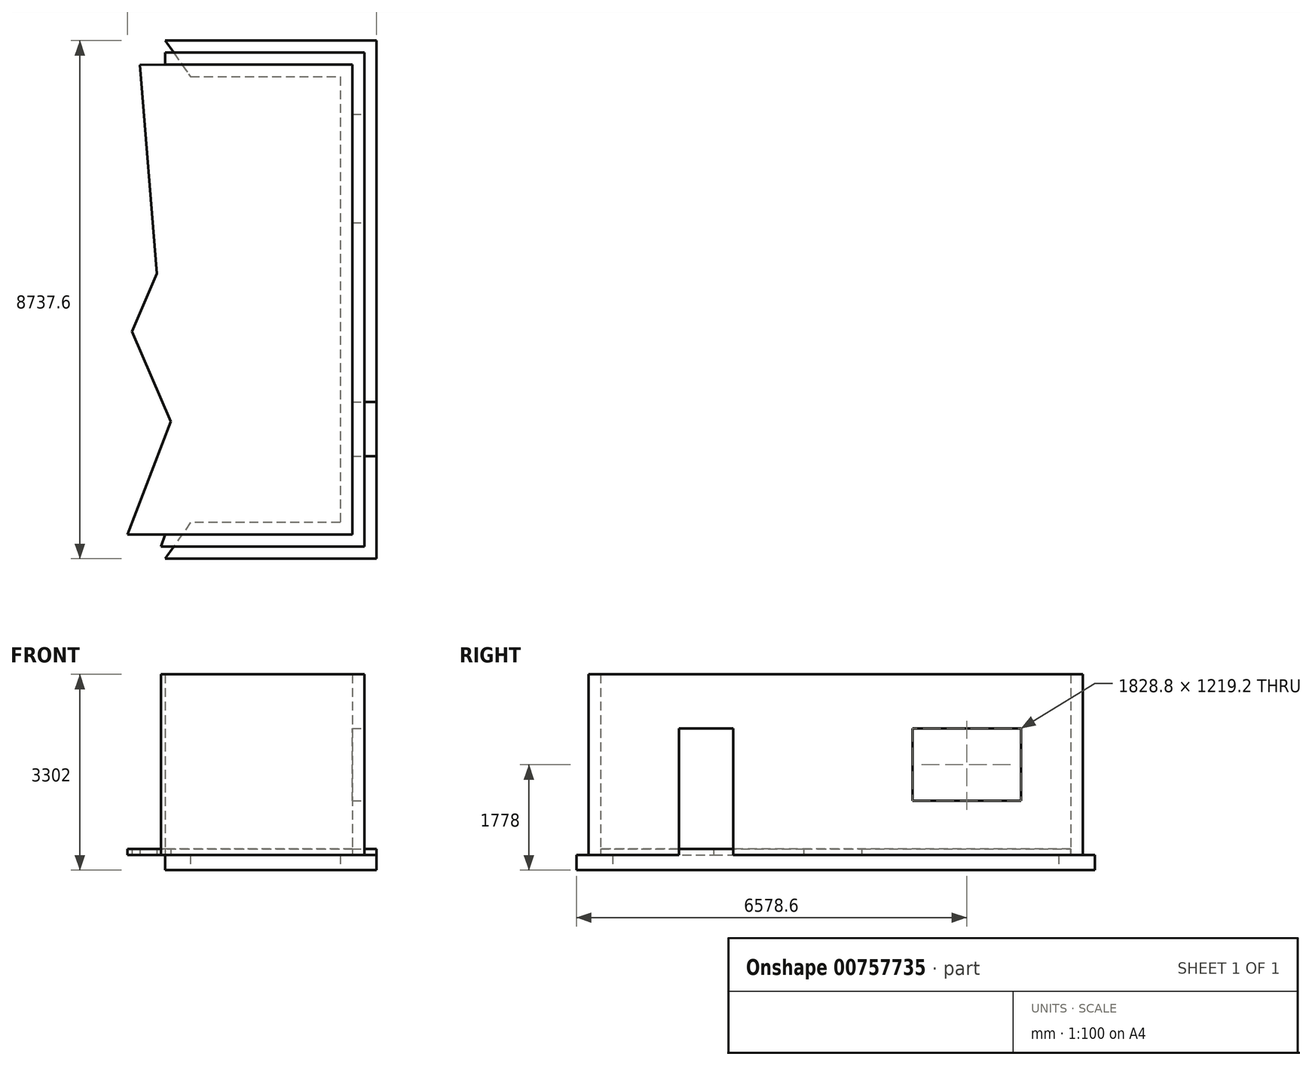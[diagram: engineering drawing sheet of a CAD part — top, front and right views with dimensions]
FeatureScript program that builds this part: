
annotation { "Feature Type Name" : "Feature", "Feature Type Description" : "" }
export const myFeature = defineFeature(function(context is Context, id is Id, definition is map)
    precondition{}
    {
        {
            var Q0;
            Q0=qCreatedBy(makeId("Top.planeOp"),FACE);
            var sketch = newSketch(context, id + "F0", { "sketchPlane" : qUnion([Q0])});
            skLineSegment(sketch, "E0", {"start": v(0, 0) * mm, "end": v(0, 8737.6) * mm});
            skLineSegment(sketch, "E1", {"start": v(0, 8737.6) * mm, "end": v(-3558.04, 8737.6) * mm});
            skLineSegment(sketch, "E2", {"start": v(-3558.04, 8737.6) * mm, "end": v(-3134.22, 8128) * mm});
            skLineSegment(sketch, "E3", {"start": v(-3134.22, 8128) * mm, "end": v(-609.6, 8128) * mm});
            skLineSegment(sketch, "E4", {"start": v(-609.6, 8128) * mm, "end": v(-609.6, 609.6) * mm});
            skLineSegment(sketch, "E5", {"start": v(-609.6, 609.6) * mm, "end": v(-3134.22, 609.6) * mm});
            skLineSegment(sketch, "E6", {"start": v(-3134.22, 609.6) * mm, "end": v(-3558.04, 0) * mm});
            skLineSegment(sketch, "E7", {"start": v(-3558.04, 0) * mm, "end": v(0, 0) * mm});
            skSolve(sketch);
        }
        {
            var Q0;
            Q0 = qSketchRegion(id + "F0", true);
            extrude(context, id + "F1", {"entities" : qUnion([Q0]), "depth" : 254 * mm, "offsetDistance" : 25.4 * mm});
        }
        {
            var Q0;
            Q0=makeQuery(id+"F1.opExtrude","CAP_FACE",FACE,{"disambiguationData":[OSD([sQuery(id+"F0.wireOp",EDGE,"E0"),sQuery(id+"F0.wireOp",EDGE,"E1"),sQuery(id+"F0.wireOp",EDGE,"E2"),sQuery(id+"F0.wireOp",EDGE,"E3"),sQuery(id+"F0.wireOp",EDGE,"E4"),sQuery(id+"F0.wireOp",EDGE,"E5"),sQuery(id+"F0.wireOp",EDGE,"E6"),sQuery(id+"F0.wireOp",EDGE,"E7")])],"isStart":false});
            var sketch = newSketch(context, id + "F2", { "sketchPlane" : qUnion([Q0])});
            skLineSegment(sketch, "E8", {"start": v(-3631.45, 203.2) * mm, "end": v(-203.2, 203.2) * mm});
            skLineSegment(sketch, "E9", {"start": v(-203.2, 203.2) * mm, "end": v(-203.2, 8534.4) * mm});
            skLineSegment(sketch, "E10", {"start": v(-203.2, 8534.4) * mm, "end": v(-3558.04, 8534.4) * mm});
            skLineSegment(sketch, "E11", {"start": v(-3558.04, 8534.4) * mm, "end": v(-3558.04, 8331.2) * mm});
            skLineSegment(sketch, "E12", {"start": v(-3558.04, 8331.2) * mm, "end": v(-406.4, 8331.2) * mm});
            skLineSegment(sketch, "E13", {"start": v(-406.4, 8331.2) * mm, "end": v(-406.4, 406.4) * mm});
            skLineSegment(sketch, "E14", {"start": v(-406.4, 406.4) * mm, "end": v(-3558.04, 406.4) * mm});
            skLineSegment(sketch, "E15", {"start": v(-3558.04, 406.4) * mm, "end": v(-3631.45, 203.2) * mm});
            skSolve(sketch);
        }
        {
            var Q0;
            Q0 = qSketchRegion(id + "F2", true);
            extrude(context, id + "F3", {"entities" : qUnion([Q0]), "operationType" : NewBodyOperationType.ADD, "depth" : 3048 * mm, "offsetDistance" : 25.4 * mm});
        }
        {
            var Q0;
            Q0=makeQuery(id+"F3.opExtrude","SWEPT_FACE",FACE,{"disambiguationData":[OSD([sQuery(id+"F2.wireOp",EDGE,"E9")])]});
            var sketch = newSketch(context, id + "F4", { "sketchPlane" : qUnion([Q0])});
            skLineSegment(sketch, "E16", {"start": v(1727.2, 254) * mm, "end": v(1727.2, 2387.6) * mm});
            skLineSegment(sketch, "E17", {"start": v(1727.2, 2387.6) * mm, "end": v(2641.6, 2387.6) * mm});
            skLineSegment(sketch, "E18", {"start": v(2641.6, 2387.6) * mm, "end": v(2641.6, 254) * mm});
            skLineSegment(sketch, "E19", {"start": v(2641.6, 254) * mm, "end": v(1727.2, 254) * mm});
            skLineSegment(sketch, "E20", {"start": v(5664.2, 2387.6) * mm, "end": v(5664.2, 1168.4) * mm});
            skLineSegment(sketch, "E21", {"start": v(5664.2, 1168.4) * mm, "end": v(7493, 1168.4) * mm});
            skLineSegment(sketch, "E22", {"start": v(7493, 1168.4) * mm, "end": v(7493, 2387.6) * mm});
            skLineSegment(sketch, "E23", {"start": v(7493, 2387.6) * mm, "end": v(5664.2, 2387.6) * mm});
            skSolve(sketch);
        }
        {
            var Q0;
            Q0 = qSketchRegion(id + "F4", true);
            extrude(context, id + "F5", {"entities" : qUnion([Q0]), "operationType" : NewBodyOperationType.REMOVE, "oppositeDirection" : true, "depth" : 203.2 * mm, "offsetDistance" : 25.4 * mm});
        }
        {
            var Q0;
            {var subQ0=sQuery(id+"F0.wireOp",EDGE,"E5");var subQ2=sQuery(id+"F0.wireOp",EDGE,"E4");var subQ3=sQuery(id+"F0.wireOp",EDGE,"E3");var subQ4=sQuery(id+"F0.wireOp",EDGE,"E2");var subQ6=sQuery(id+"F0.wireOp",EDGE,"E6");var subQ14=sQuery(id+"F0.wireOp",EDGE,"E7");var subQ15=sQuery(id+"F0.wireOp",EDGE,"E1");var subQ16=sQuery(id+"F0.wireOp",EDGE,"E0");var subQ17=makeQuery(id+"F1.opExtrude","CAP_FACE",FACE,{"disambiguationData":[OSD([subQ16,subQ15,subQ4,subQ3,subQ2,subQ0,subQ6,subQ14])],"isStart":false});Q0=makeQuery(id+"F5.boolean.opBoolean","MERGE",FACE,{"derivedFrom":[makeQuery(id+"F3.boolean.opBoolean","SPLIT",FACE,{"disambiguationData":[TD([makeQuery(id+"F1.opExtrude","SWEPT_FACE",FACE,{"disambiguationData":[OSD([subQ16])]})])],"derivedFrom":subQ17}),makeQuery(id+"F3.boolean.opBoolean","SPLIT",FACE,{"disambiguationData":[TD([makeQuery(id+"F1.opExtrude","SWEPT_FACE",FACE,{"disambiguationData":[OSD([subQ3])]})])],"derivedFrom":subQ17}),makeQuery(id+"F5.opExtrude","SWEPT_FACE",FACE,{"disambiguationData":[OSD([sQuery(id+"F4.wireOp",EDGE,"E19")])]})]});}
            var sketch = newSketch(context, id + "F6", { "sketchPlane" : qUnion([Q0])});
            skLineSegment(sketch, "E24", {"start": v(-406.4, 406.4) * mm, "end": v(-4197.9, 406.4) * mm});
            skLineSegment(sketch, "E25", {"start": v(-4197.9, 406.4) * mm, "end": v(-3467.95, 2315.71) * mm});
            skLineSegment(sketch, "E26", {"start": v(-3467.95, 2315.71) * mm, "end": v(-4117.45, 3829.05) * mm});
            skLineSegment(sketch, "E27", {"start": v(-4117.45, 3829.05) * mm, "end": v(-3701.4, 4810.41) * mm});
            skLineSegment(sketch, "E28", {"start": v(-3701.4, 4810.41) * mm, "end": v(-3988.06, 8325.82) * mm});
            skLineSegment(sketch, "E29", {"start": v(-3988.06, 8325.82) * mm, "end": v(-406.4, 8331.2) * mm});
            skLineSegment(sketch, "E30", {"start": v(-406.4, 8331.2) * mm, "end": v(-406.4, 2641.6) * mm});
            skLineSegment(sketch, "E31", {"start": v(-406.4, 2641.6) * mm, "end": v(0, 2641.6) * mm});
            skLineSegment(sketch, "E32", {"start": v(0, 2641.6) * mm, "end": v(0, 1727.2) * mm});
            skLineSegment(sketch, "E33", {"start": v(0, 1727.2) * mm, "end": v(-406.4, 1727.2) * mm});
            skLineSegment(sketch, "E34", {"start": v(-406.4, 1727.2) * mm, "end": v(-406.4, 406.4) * mm});
            skSolve(sketch);
        }
        {
            var Q0;
            Q0 = qSketchRegion(id + "F6", true);
            extrude(context, id + "F7", {"entities" : qUnion([Q0]), "operationType" : NewBodyOperationType.ADD, "depth" : 101.6 * mm, "offsetDistance" : 25.4 * mm});
        }
    });
